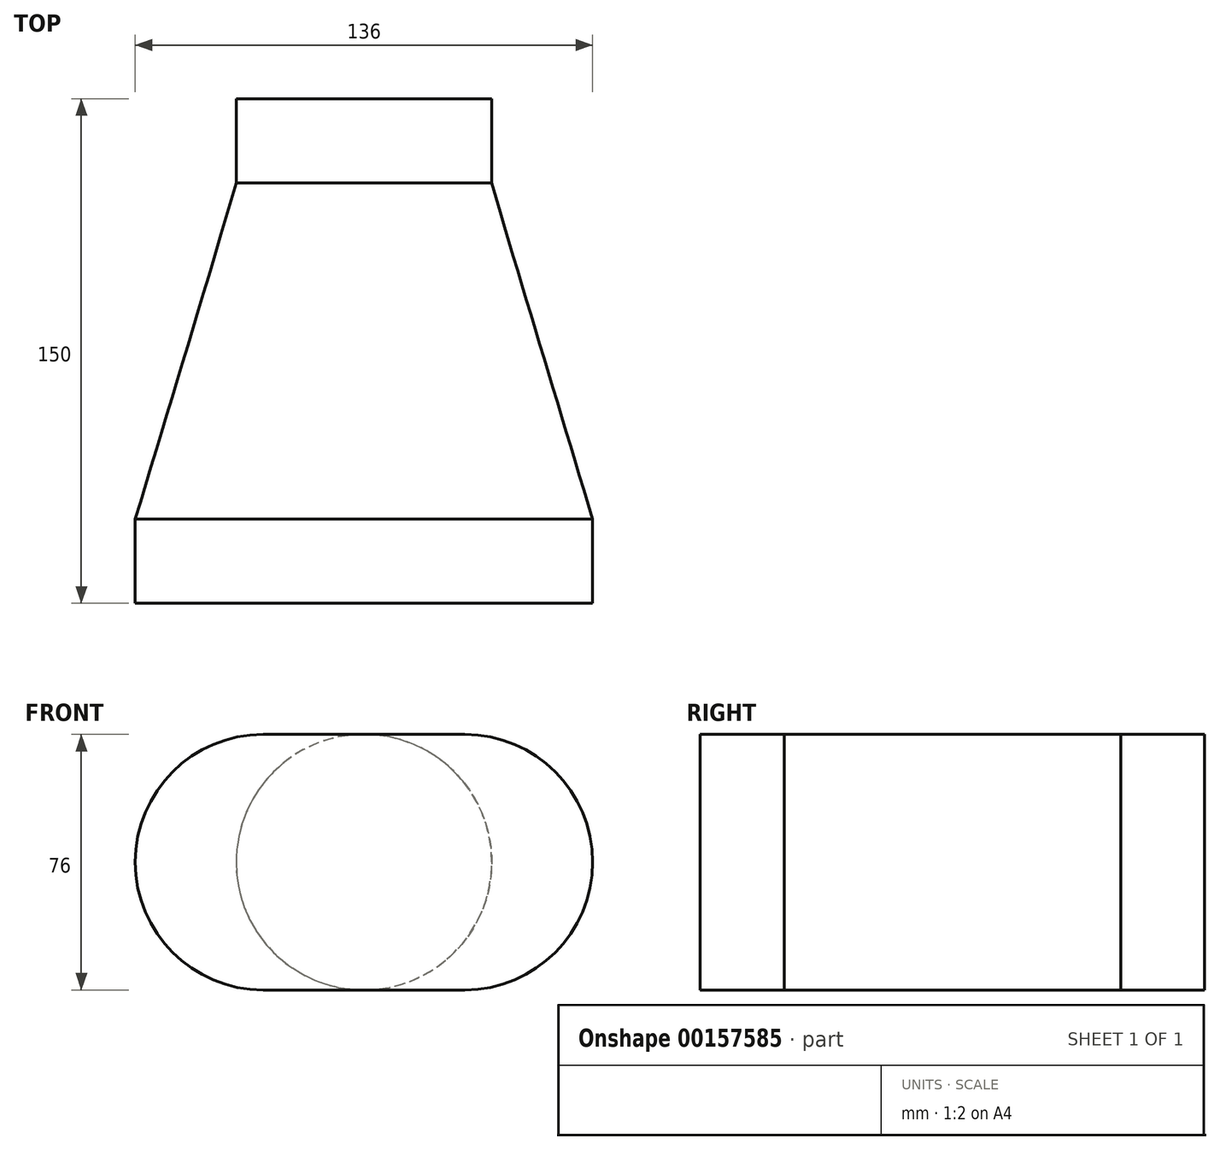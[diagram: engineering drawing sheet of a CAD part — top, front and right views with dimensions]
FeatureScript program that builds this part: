
annotation { "Feature Type Name" : "Feature", "Feature Type Description" : "" }
export const myFeature = defineFeature(function(context is Context, id is Id, definition is map)
    precondition{}
    {
        {
            assignVariable(context, id + "F0", {"name" : "Length", "anyValue" : 100});
        }
        {
            var Q0;
            Q0=qCreatedBy(makeId("Front.planeOp"),FACE);
            cPlane(context, id + "F1", {"entities" : qUnion([Q0]), "cplaneType" : CPlaneType.OFFSET, "offset" : (getVariable(context, 'Length')) * mm, "width" : 150 * mm, "height" : 150 * mm});
        }
        {
            var Q0;
            Q0=qCreatedBy(makeId("Front.planeOp"),FACE);
            var sketch = newSketch(context, id + "F2", { "sketchPlane" : qUnion([Q0])});
            skCircle(sketch, "E0", {"center": v(0, 0) * mm, "radius": 38 * mm});
            skLineSegment(sketch, "E1", {"start": v(0, 38) * mm, "end": v(-30, 38) * mm});
            skLineSegment(sketch, "E2", {"start": v(-30, 38) * mm, "end": v(-30, -39.64) * mm, "construction": true});
            skLineSegment(sketch, "E3", {"start": v(0, -38) * mm, "end": v(-30, -38) * mm});
            skArc(sketch, "E4", {"start": v(-30, 38) * mm, "mid": v(-68, 0) * mm, "end": v(-30, -38) * mm});
            skLineSegment(sketch, "E5.MirrorCS", {"start": v(0, 38) * mm, "end": v(30, 38) * mm});
            skArc(sketch, "E6.MirrorCS", {"start": v(30, 38) * mm, "mid": v(68, 0) * mm, "end": v(30, -38) * mm});
            skLineSegment(sketch, "E7.MirrorCS", {"start": v(0, -38) * mm, "end": v(30, -38) * mm});
            skSolve(sketch);
        }
        {
            var Q0;
            Q0=qCreatedBy(id+"F1.planeOp",FACE);
            var sketch = newSketch(context, id + "F3", { "sketchPlane" : qUnion([Q0])});
            skLineSegment(sketch, "E8.0", {"start": v(0, 38) * mm, "end": v(-30, 38) * mm});
            skArc(sketch, "E9.0", {"start": v(-30, 38) * mm, "mid": v(-68, 0) * mm, "end": v(-30, -38) * mm});
            skLineSegment(sketch, "E10.0", {"start": v(0, -38) * mm, "end": v(-30, -38) * mm});
            skLineSegment(sketch, "E11.0", {"start": v(0, -38) * mm, "end": v(30, -38) * mm});
            skArc(sketch, "E12.0", {"start": v(30, 38) * mm, "mid": v(68, 0) * mm, "end": v(30, -38) * mm});
            skLineSegment(sketch, "E13.0", {"start": v(0, 38) * mm, "end": v(30, 38) * mm});
            skSolve(sketch);
        }
        {
            var Q0;
            {var subQ0=sQuery(id+"F2.wireOp",EDGE,"E0");var subQ1=makeQuery(id+"F2.imprint","INTERSECT",VERTEX,{"derivedFrom":[subQ0,sQuery(id+"F2.wireOp",EDGE,"E1"),sQuery(id+"F2.wireOp",EDGE,"E5.MirrorCS")]});Q0=makeQuery(id+"F2.imprint","IMPRINT",FACE,{"disambiguationData":[TD([[makeQuery(id+"F2.imprint","IMPRINT",EDGE,{"disambiguationData":[TD([[subQ1,-1.0]])],"derivedFrom":subQ0}),1.0]])]});}
            extrude(context, id + "F4", {"entities" : qUnion([Q0]), "oppositeDirection" : true, "depth" : 25 * mm});
        }
        {
            var Q0;
            Q0=makeQuery(id+"F3.imprint","IMPRINT",FACE,{"disambiguationData":[TD([[makeQuery(id+"F3.imprint","IMPRINT",EDGE,{"derivedFrom":sQuery(id+"F3.wireOp",EDGE,"E8.0")}),1.0]])]});
            extrude(context, id + "F5", {"entities" : qUnion([Q0]), "depth" : 25 * mm});
        }
        {
            var Q1;
            Q1=makeQuery(id+"F4.opExtrude","CAP_FACE",FACE,{"disambiguationData":[OSD([sQuery(id+"F2.wireOp",EDGE,"E0")])],"isStart":true});
            var Q2;
            Q2=makeQuery(id+"F5.opExtrude","CAP_FACE",FACE,{"disambiguationData":[OSD([sQuery(id+"F3.wireOp",EDGE,"E8.0"),sQuery(id+"F3.wireOp",EDGE,"E9.0"),sQuery(id+"F3.wireOp",EDGE,"E10.0"),sQuery(id+"F3.wireOp",EDGE,"E11.0"),sQuery(id+"F3.wireOp",EDGE,"E12.0"),sQuery(id+"F3.wireOp",EDGE,"E13.0")])],"isStart":true});
            loft(context, id + "F6", {"operationType" : NewBodyOperationType.ADD, "sheetProfilesArray" : [{ "sheetProfileEntities" : qUnion([Q1]) }, { "sheetProfileEntities" : qUnion([Q2]) }]});
        }
    });
